# Revit family: HARMANN - REVIT - MAXEE_EC- poziomy
name_source: partatom
category: Wyposażenie mechaniczne
units: mm (PartAtom-declared; Revit-internal decimal feet)

## family parameters
Klasyfikacja = Brak
Obiekt nadrzędny = Powierzchnia
Punkt obliczania pomieszczeń = Nie
Tnij formami wycięć po wczytaniu = Nie
Typ części = Normalny
Współdzielony = Nie
Wymiar okrągłego złącza = Użyj średnicy
Zachowaj orientację opisów = Nie

## types (5) — shared parameters
Autor = https://www.archispace.com
Domyślna rzędna = 1219.2 mm
Lookup Table Name = MAXEE EC
Opis = Kanałowy wentylator bytowy
Producent = Harmann Polska Sp. z o.o.
Temperatura pracy T = 60 °C
Wysokość FSD = 57 mm  [stored 0.187008 ft]
Zasilanie Ilość faz = 1
Zasilanie fmax = 10 V
Zasilanie fmin = 1 V
Zasilanie napięcie nominalne Unom = 230 V

## per-type parameters (varying)
- MAXEE 315/5100EC: A=380 mm  [stored 1.24672 ft]; Akc ESD=HARMANN - Akcesoria - ESD : ESD 315; Akc EXP=HARMANN - Akcesoria - EXP : EXP 315; Akc FAL=HARMANN - Akcesoria - FAL : FAL 315; Akc FSD=HARMANN - Akcesoria - FSD : FSD 01; Akc RAF=HARMANN - Akcesoria - RAF : RAF 315; Akc RVK H=HARMANN - Akcesoria - RVK H : RVK H 315; Akc RVS=HARMANN - Akcesoria - RVS : RVS 315; Akc SGE=HARMANN - Akcesoria - SGE : SGE 315; Akc SGE dla ESD=HARMANN - Akcesoria - SGE : SGE 355; B=383 mm  [stored 1.25656 ft]; C=355 mm; Ciśnienie akustyczne nominalne obudowa Lpa=68 dB(A); D=315 mm  [stored 1.03346 ft]; D2=321 mm  [stored 1.05315 ft]; Długość MAXEE=383 mm  [stored 1.25656 ft]; F=396 mm  [stored 1.29921 ft]; Klasa odporności ogniowej Tmax=Brak; MAXEE_EC=HARMANN - MAXEE : MAXEE 315/5100EC; Masa=18.50 kg; Moc akustyczna nominalna obudowa Lwa=75 dB(A); Model=MAXEE 315/5100EC; N1=2  [stored 0.00656168 ft]; Numer artykułu=15413600; Obroty nominalne nnom=3010.000 obr./min; Powietrze Przepływ Maksymalny Qmax=5150.0 m³/h; Powietrze ciśnienie statyczne maksymalne dPmax=390.0 Pa; R2=157.5 mm  [stored 0.516732 ft]; Wysokość=116.5 mm; Wysokość FAL=98 mm  [stored 0.321522 ft]; Zasilanie Moc maksymalna Pmax=900 W; Zasilanie natężenie maksymalne Imax=5 A
- MAXEE 355/7100EC: A=420 mm  [stored 1.37795 ft]; Akc ESD=HARMANN - Akcesoria - ESD : ESD 355; Akc EXP=HARMANN - Akcesoria - EXP : EXP 355; Akc FAL=HARMANN - Akcesoria - FAL : FAL 355; Akc FSD=HARMANN - Akcesoria - FSD : FSD 01; Akc RAF=HARMANN - Akcesoria - RAF : RAF 355; Akc RVK H=HARMANN - Akcesoria - RVK H : RVK H 355; Akc RVS=HARMANN - Akcesoria - RVS : RVS 355; Akc SGE=HARMANN - Akcesoria - SGE : SGE 355; Akc SGE dla ESD=HARMANN - Akcesoria - SGE : SGE 400; B=383 mm  [stored 1.25656 ft]; C=395 mm  [stored 1.29593 ft]; Ciśnienie akustyczne nominalne obudowa Lpa=72 dB(A); D=355 mm; D2=361 mm  [stored 1.18438 ft]; Długość MAXEE=383 mm  [stored 1.25656 ft]; F=396 mm  [stored 1.29921 ft]; Klasa odporności ogniowej Tmax=brak; MAXEE_EC=HARMANN - MAXEE : MAXEE 355/7100EC; Masa=22.20 kg; Moc akustyczna nominalna obudowa Lwa=79 dB(A); Model=MAXEE 355/7100EC; N1=4  [stored 0.0131234 ft]; Numer artykułu=15412700; Obroty nominalne nnom=3000.000 obr./min; Powietrze Przepływ Maksymalny Qmax=7155.0 m³/h; Powietrze ciśnienie statyczne maksymalne dPmax=500.0 Pa; R2=177.5 mm  [stored 0.582349 ft]; Wysokość=136 mm; Wysokość FAL=99 mm  [stored 0.324803 ft]; Zasilanie Moc maksymalna Pmax=1648 W; Zasilanie natężenie maksymalne Imax=9 A
- MAXEE 400/8900EC: A=480 mm  [stored 1.5748 ft]; Akc ESD=HARMANN - Akcesoria - ESD : ESD 400; Akc EXP=HARMANN - Akcesoria - EXP : EXP 400; Akc FAL=HARMANN - Akcesoria - FAL : FAL 400; Akc FSD=HARMANN - Akcesoria - FSD : FSD 02; Akc RAF=HARMANN - Akcesoria - RAF : RAF 400; Akc RVK H=HARMANN - Akcesoria - RVK H : RVK H 400; Akc RVS=HARMANN - Akcesoria - RVS : RVS 400; Akc SGE=HARMANN - Akcesoria - SGE : SGE 400; Akc SGE dla ESD=HARMANN - Akcesoria - SGE : SGE 450; B=368 mm  [stored 1.20735 ft]; C=450 mm  [stored 1.47638 ft]; Ciśnienie akustyczne nominalne obudowa Lpa=72 dB(A); D=400 mm  [stored 1.31234 ft]; D2=406 mm  [stored 1.33202 ft]; Długość MAXEE=368 mm  [stored 1.20735 ft]; F=396 mm  [stored 1.29921 ft]; Klasa odporności ogniowej Tmax=brak; MAXEE_EC=HARMANN - MAXEE : MAXEE 400/8900EC; Masa=20.40 kg; Moc akustyczna nominalna obudowa Lwa=79 dB(A); Model=MAXEE 400/8900EC; N1=6  [stored 0.019685 ft]; Numer artykułu=15409300; Obroty nominalne nnom=26100.000 obr./min; Powietrze Przepływ Maksymalny Qmax=8900.0 m³/h; Powietrze ciśnienie statyczne maksymalne dPmax=510.0 Pa; R2=200 mm  [stored 0.656168 ft]; Wysokość=158.5 mm  [stored 0.520013 ft]; Wysokość FAL=99 mm  [stored 0.324803 ft]; Zasilanie Moc maksymalna Pmax=1460 W; Zasilanie natężenie maksymalne Imax=10 A
- MAXEE 450/11100EC: A=530 mm  [stored 1.73885 ft]; Akc ESD=HARMANN - Akcesoria - ESD : ESD 450; Akc EXP=HARMANN - Akcesoria - EXP : EXP 450; Akc FAL=HARMANN - Akcesoria - FAL : FAL 450; Akc FSD=HARMANN - Akcesoria - FSD : FSD 02; Akc RAF=HARMANN - Akcesoria - RAF : RAF 450; Akc RVK H=HARMANN - Akcesoria - RVK H : RVK H 450; Akc RVS=HARMANN - Akcesoria - RVS : RVS 450; Akc SGE=HARMANN - Akcesoria - SGE : SGE 450; Akc SGE dla ESD=HARMANN - Akcesoria - SGE : SGE 500; B=368 mm  [stored 1.20735 ft]; C=500 mm  [stored 1.64042 ft]; Ciśnienie akustyczne nominalne obudowa Lpa=60 dB(A); D=450 mm  [stored 1.47638 ft]; D2=456 mm  [stored 1.49606 ft]; Długość MAXEE=368 mm  [stored 1.20735 ft]; F=396 mm  [stored 1.29921 ft]; Klasa odporności ogniowej Tmax=brak; MAXEE_EC=HARMANN - MAXEE : MAXEE 450/11100EC; Masa=32.80 kg; Moc akustyczna nominalna obudowa Lwa=67 dB(A); Model=MAXEE 450/11100EC; N1=7  [stored 0.0229659 ft]; Numer artykułu=15411300; Obroty nominalne nnom=1510.000 obr./min; Powietrze Przepływ Maksymalny Qmax=9860.0 m³/h; Powietrze ciśnienie statyczne maksymalne dPmax=260.0 Pa; R2=225 mm  [stored 0.738189 ft]; Wysokość=183.5 mm; Wysokość FAL=99 mm  [stored 0.324803 ft]; Zasilanie Moc maksymalna Pmax=1164 W; Zasilanie natężenie maksymalne Imax=6 A
- MAXEE 500/9800EC: A=590 mm  [stored 1.9357 ft]; Akc ESD=HARMANN - Akcesoria - ESD : ESD 500; Akc EXP=HARMANN - Akcesoria - EXP : EXP 500; Akc FAL=HARMANN - Akcesoria - FAL : FAL 500; Akc FSD=HARMANN - Akcesoria - FSD : FSD 02; Akc RAF=HARMANN - Akcesoria - RAF : RAF 500; Akc RVK H=HARMANN - Akcesoria - RVK H : RVK H 500; Akc RVS=HARMANN - Akcesoria - RVS : RVS 500; Akc SGE=HARMANN - Akcesoria - SGE : SGE 500; Akc SGE dla ESD=HARMANN - Akcesoria - SGE : SGE 560; B=443 mm  [stored 1.45341 ft]; C=560 mm  [stored 1.83727 ft]; Ciśnienie akustyczne nominalne obudowa Lpa=64 dB(A); D=500 mm  [stored 1.64042 ft]; D2=506 mm  [stored 1.6601 ft]; Długość MAXEE=443 mm  [stored 1.45341 ft]; F=465 mm  [stored 1.52559 ft]; Klasa odporności ogniowej Tmax=brak; MAXEE_EC=HARMANN - MAXEE : MAXEE 500/9800EC; Masa=38.50 kg; Moc akustyczna nominalna obudowa Lwa=71 dB(A); Model=MAXEE 500/4/11600T; N1=9  [stored 0.0295276 ft]; Numer artykułu=15411100; Obroty nominalne nnom=1760.000 obr./min; Powietrze Przepływ Maksymalny Qmax=11640.0 m³/h; Powietrze ciśnienie statyczne maksymalne dPmax=360.0 Pa; R2=250 mm  [stored 0.82021 ft]; Wysokość=208.5 mm; Wysokość FAL=99 mm  [stored 0.324803 ft]; Zasilanie Moc maksymalna Pmax=1820 W; Zasilanie natężenie maksymalne Imax=3 A

note: [stored X ft] marks values corroborated as IEEE doubles in the binary element streams (Revit-internal decimal feet)

## geometry (parser evidence)
native form markers: Sweep x29
no freeform markers — native parametric forms only
